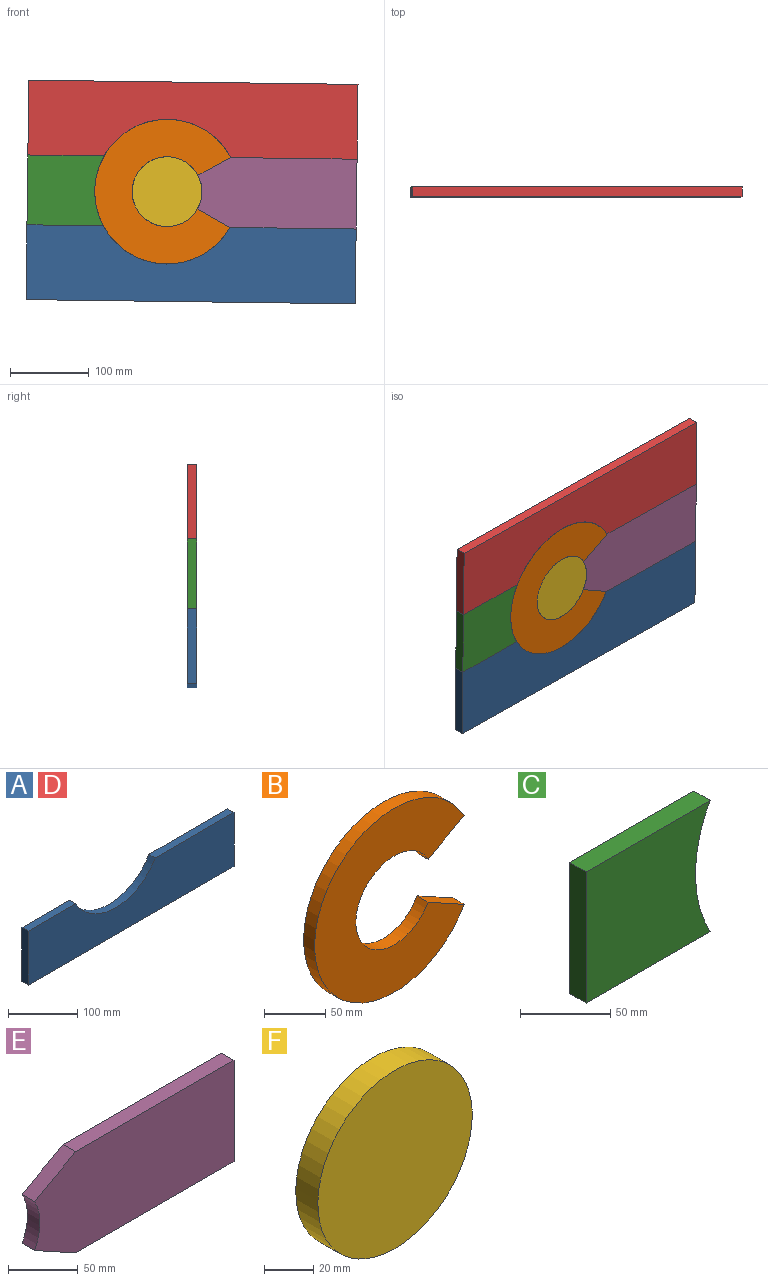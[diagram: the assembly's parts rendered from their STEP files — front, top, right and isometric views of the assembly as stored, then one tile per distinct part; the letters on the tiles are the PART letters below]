
ASSEMBLY  parts=6 mates=14
PART A: 8 faces, bbox 419.1x12.7x95.3 mm
  f0: plane 95.25x12.7mm, normal (-1,0,0), area 1209.7mm2, adj f1,f5,f6,f7
  f1: plane 419.1x12.7mm, normal (0,0,-1), area 5322.6mm2, adj f0,f2,f6,f7
  f2: plane 95.25x12.7mm, normal (1,0,0), area 1209.7mm2, adj f1,f3,f6,f7
  f3: plane 160.67x12.7mm, normal (0,0,1), area 2040.4mm2, adj f2,f4,f6,f7
  f4: cylinder r=92.08mm len=161.27mm, axis (0,1,0), area 2495.4mm2, adj f3,f5,f6,f7
  f5: plane 97.17x12.7mm, normal (0,0,1), area 1234mm2, adj f0,f4,f6,f7
  f6: plane 419.1x95.25mm, normal (0,-1,0), area 34457.7mm2, adj f0,f1,f2,f3,f4,f5
  f7: plane 419.1x95.25mm, normal (0,1,0), area 34457.7mm2, adj f0,f1,f2,f3,f4,f5
PART B: 6 faces, bbox 172.7x12.7x184.2 mm
  f0: cylinder r=44.45mm len=88.9mm, axis (0,1,0), area 2978.1mm2, adj f1,f3,f4,f5
  f1: plane 41.71x22.99mm, normal (0.48,0,-0.88), area 604.8mm2, adj f0,f2,f4,f5
  f2: cylinder r=92.08mm len=184.15mm, axis (0,1,0), area 6169mm2, adj f1,f3,f4,f5
  f3: plane 41.71x22.99mm, normal (0.48,0,0.88), area 604.8mm2, adj f0,f2,f4,f5
  f4: plane 184.15x172.71mm, normal (0,-1,0), area 17150.9mm2, adj f0,f1,f2,f3
  f5: plane 184.15x172.71mm, normal (0,1,0), area 17150.9mm2, adj f0,f1,f2,f3
PART C: 6 faces, bbox 97.2x12.7x88.9 mm
  f0: plane 88.9x12.7mm, normal (-1,0,0), area 1129mm2, adj f1,f3,f4,f5
  f1: plane 97.17x12.7mm, normal (0,0,-1), area 1234mm2, adj f0,f2,f4,f5
  f2: cylinder r=92.08mm len=88.9mm, axis (0,1,0), area 1178.2mm2, adj f1,f3,f4,f5
  f3: plane 97.17x12.7mm, normal (0,0,1), area 1234mm2, adj f0,f2,f4,f5
  f4: plane 97.17x88.9mm, normal (0,-1,0), area 7951.1mm2, adj f0,f1,f2,f3
  f5: plane 97.17x88.9mm, normal (0,1,0), area 7951.1mm2, adj f0,f1,f2,f3
PART D: same geometry as A
PART E: 8 faces, bbox 202.4x12.7x88.9 mm
  f0: plane 160.67x12.7mm, normal (0,0,-1), area 2040.4mm2, adj f1,f5,f6,f7
  f1: plane 88.9x12.7mm, normal (1,0,0), area 1129mm2, adj f0,f2,f6,f7
  f2: plane 160.67x12.7mm, normal (0,0,1), area 2040.4mm2, adj f1,f3,f6,f7
  f3: plane 41.71x22.99mm, normal (-0.48,0,0.88), area 604.8mm2, adj f2,f4,f6,f7
  f4: cylinder r=44.45mm len=42.92mm, axis (0,1,0), area 568.8mm2, adj f3,f5,f6,f7
  f5: plane 41.71x22.99mm, normal (-0.48,0,-0.88), area 604.8mm2, adj f0,f4,f6,f7
  f6: plane 202.37x88.9mm, normal (0,-1,0), area 16871.9mm2, adj f0,f1,f2,f3,f4,f5
  f7: plane 202.37x88.9mm, normal (0,1,0), area 16871.9mm2, adj f0,f1,f2,f3,f4,f5
PART F: 3 faces, bbox 88.9x12.7x88.9 mm
  f0: cylinder r=44.45mm len=88.9mm, axis (0,1,0), area 3547mm2, adj f1,f2
  f1: plane 88.9x88.9mm, normal (0,-1,0), area 6207.2mm2, adj f0
  f2: plane 88.9x88.9mm, normal (0,1,0), area 6207.2mm2, adj f0
PLACE A rot(axis=(0,1,0),0.7deg) t=(30.57,12.7,-92.47)mm
PLACE B rot(axis=(0,1,0),0.7deg) t=(0,12.7,0)mm
PLACE C rot(axis=(0,1,0),0.7deg) t=(-126.99,12.7,1.63)mm
PLACE D rot(axis=(-1,0,0.01),180deg) t=(32.93,0,91.66)mm
PLACE E rot(axis=(0,1,0),0.7deg) t=(120.64,12.7,-1.55)mm
PLACE F t=(0,12.7,0)mm
MATE planar D.f7 <-> B.f2  axis (0,-1,0) through (38.02,0,96.05)mm
MATE cylindrical E.f4 <-> F.f0  axis (0,1,0) through (0,6.35,0)mm
MATE parallel E.f2 <-> C.f3  axis (0.01,0,1) through (81.2,12.7,43.41)mm
MATE parallel B.f1 <-> E.f3  axis (0.47,0,-0.88) through (60.2,6.35,32.18)mm
MATE cylindrical A.f4 <-> B.f2  axis (0,1,0) through (0,6.35,0)mm
MATE parallel D.f3 <-> E.f2  axis (-0.01,0,-1) through (161.52,6.35,42.38)mm
MATE cylindrical C.f2 <-> B.f2  axis (0,1,0) through (0,6.35,0)mm
MATE planar F.f0 <-> B.f4  axis (0,-1,0) through (0,0,0)mm
MATE planar C.f4 <-> B.f0  axis (0,-1,0) through (-133.01,0,1.71)mm
MATE planar E.f6 <-> F.f0  axis (0,-1,0) through (146,0,-1.87)mm
MATE planar A.f6 <-> F.f0  axis (0,-1,0) through (35.54,0,-96.99)mm
MATE parallel E.f0 <-> A.f3  axis (-0.01,0,-1) through (80.06,0,-45.48)mm
MATE cylindrical D.f4 <-> B.f2  axis (0,-1,0) through (0,6.35,0)mm
MATE cylindrical F.f0 <-> B.f0  axis (0,1,0) through (0,12.7,0)mm
